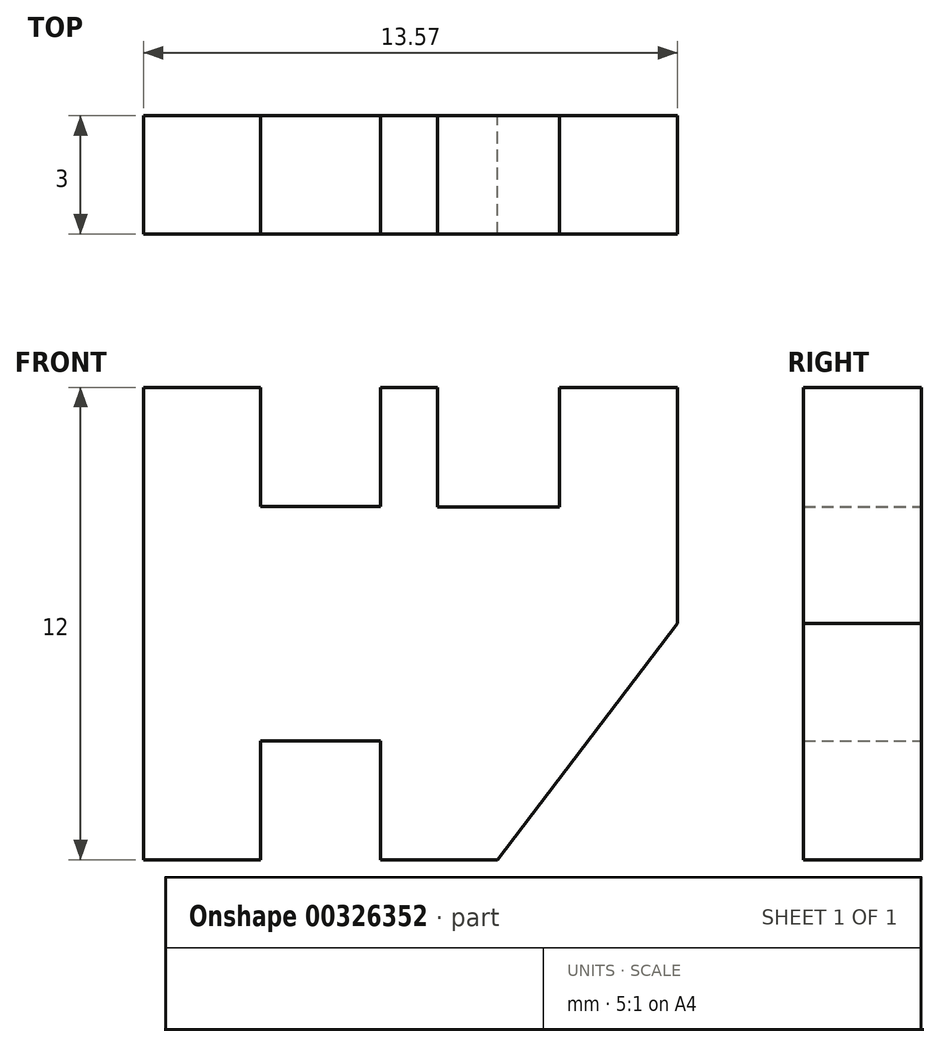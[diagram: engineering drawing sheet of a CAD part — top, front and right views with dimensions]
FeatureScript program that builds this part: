
annotation { "Feature Type Name" : "Feature", "Feature Type Description" : "" }
export const myFeature = defineFeature(function(context is Context, id is Id, definition is map)
    precondition{}
    {
        {
            var Q0;
            Q0=qCreatedBy(makeId("Front.planeOp"),FACE);
            var sketch = newSketch(context, id + "F0", { "sketchPlane" : qUnion([Q0])});
            skLineSegment(sketch, "E0", {"start": v(4.5, 0) * mm, "end": v(1.52, 0) * mm});
            skLineSegment(sketch, "E1", {"start": v(1.52, 0) * mm, "end": v(1.52, 3.02) * mm});
            skLineSegment(sketch, "E2", {"start": v(1.52, 3.02) * mm, "end": v(-1.52, 3.02) * mm});
            skLineSegment(sketch, "E3", {"start": v(-1.52, 3.02) * mm, "end": v(-1.52, 0) * mm});
            skLineSegment(sketch, "E4", {"start": v(-1.52, 0) * mm, "end": v(-4.5, 0) * mm});
            skLineSegment(sketch, "E5", {"start": v(-4.5, 0) * mm, "end": v(-4.5, 12) * mm});
            skLineSegment(sketch, "E6", {"start": v(-4.5, 12) * mm, "end": v(-1.52, 12) * mm});
            skLineSegment(sketch, "E7", {"start": v(-1.52, 12) * mm, "end": v(-1.52, 8.98) * mm});
            skLineSegment(sketch, "E8", {"start": v(-1.52, 8.98) * mm, "end": v(1.52, 8.98) * mm});
            skLineSegment(sketch, "E9", {"start": v(1.52, 8.98) * mm, "end": v(1.52, 12) * mm});
            skLineSegment(sketch, "E10", {"start": v(1.52, 12) * mm, "end": v(2.97, 12) * mm});
            skPoint(sketch, "E11", {"position": v(2.97, 12) * mm});
            skPoint(sketch, "E12", {"position": v(2.97, 0) * mm});
            skPoint(sketch, "E13", {"position": v(6.07, 12) * mm});
            skPoint(sketch, "E14.orphan", {"position": v(4.5, 12) * mm});
            skLineSegment(sketch, "E15", {"start": v(6.07, 12) * mm, "end": v(9.07, 12) * mm});
            skLineSegment(sketch, "E16", {"start": v(9.07, 12) * mm, "end": v(9.07, 6) * mm});
            skLineSegment(sketch, "E17", {"start": v(9.07, 6) * mm, "end": v(4.5, 0) * mm});
            skLineSegment(sketch, "E18", {"start": v(2.97, 12) * mm, "end": v(2.97, 8.96) * mm});
            skLineSegment(sketch, "E19", {"start": v(2.97, 8.96) * mm, "end": v(6.07, 8.96) * mm});
            skLineSegment(sketch, "E20", {"start": v(6.07, 8.96) * mm, "end": v(6.07, 12) * mm});
            skSolve(sketch);
        }
        {
            var Q0;
            Q0=makeQuery(id+"F0.imprint","IMPRINT",FACE,{"disambiguationData":[TD([[makeQuery(id+"F0.imprint","IMPRINT",EDGE,{"derivedFrom":sQuery(id+"F0.wireOp",EDGE,"1RVhYwTr-rsvK-3Hkf-gFhk-pf0AGQm3IdGA")}),-1.0]])]});
            var Q1;
            Q1=makeQuery(id+"F0.imprint","IMPRINT",FACE,{"disambiguationData":[TD([[makeQuery(id+"F0.imprint","IMPRINT",EDGE,{"derivedFrom":sQuery(id+"F0.wireOp",EDGE,"E0")}),-1.0]])]});
            extrude(context, id + "F1", {"entities" : qUnion([Q0, Q1]), "depth" : 3 * mm});
        }
    });
